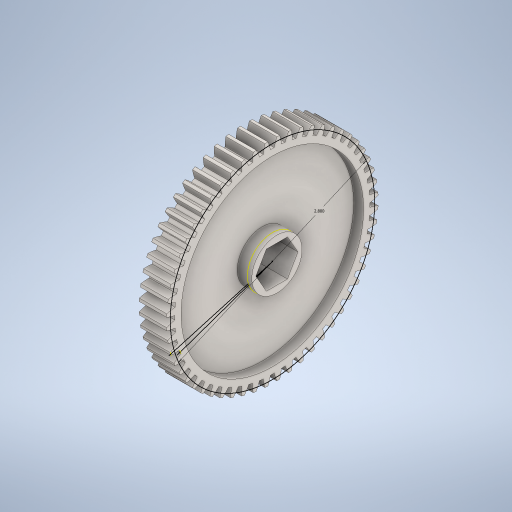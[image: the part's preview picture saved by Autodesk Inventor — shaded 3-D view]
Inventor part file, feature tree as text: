
AUTODESK INVENTOR PART (.ipt)
format: ipt  version: 2023 (Build 270158030, 158C)  size: 528,896 bytes
history: native  units: in
note: dims shown in document units (in); Inventor stores cm internally (conversion verified against a paired STEP export)
features: sketch x1, other x1
ambient origin geometry x8: Origin, YZ Plane, XZ Plane, XY Plane, X Axis, Y Axis, Z Axis, Center Point
bodies: Solid1 (feature_tree)
feature tree (2):
  sketch  "Sketch1"  dims[d0=2.8in]
  other  "Bore"
